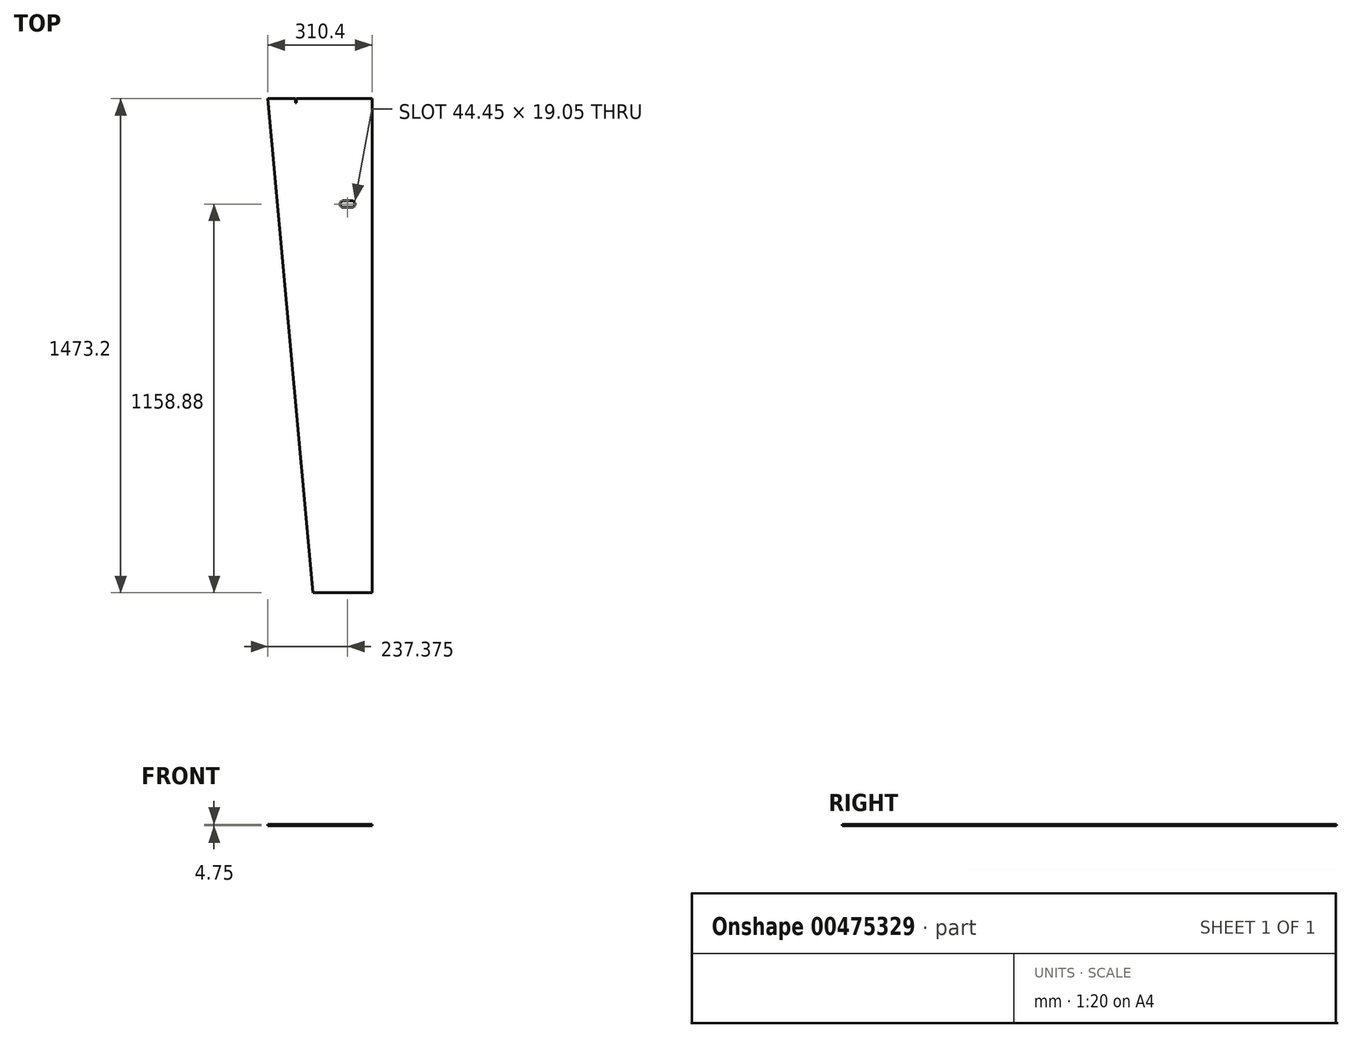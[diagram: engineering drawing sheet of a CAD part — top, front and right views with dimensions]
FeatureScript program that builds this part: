
annotation { "Feature Type Name" : "Feature", "Feature Type Description" : "" }
export const myFeature = defineFeature(function(context is Context, id is Id, definition is map)
    precondition{}
    {
        {
            var Q0;
            Q0=qCreatedBy(makeId("Top.planeOp"),FACE);
            var sketch = newSketch(context, id + "F0", { "sketchPlane" : qUnion([Q0])});
            skLineSegment(sketch, "E0", {"start": v(-176.47, -736.6) * mm, "end": v(-310.4, 736.6) * mm});
            skLineSegment(sketch, "E1", {"start": v(-310.4, 736.6) * mm, "end": v(-228.6, 736.6) * mm});
            skLineSegment(sketch, "E2", {"start": v(0, 736.6) * mm, "end": v(0, -736.6) * mm});
            skLineSegment(sketch, "E3", {"start": v(0, -736.6) * mm, "end": v(-176.47, -736.6) * mm});
            skLineSegment(sketch, "E4.bottom", {"start": v(-85.73, 431.8) * mm, "end": v(-60.33, 431.8) * mm});
            skLineSegment(sketch, "E4.top", {"start": v(-85.73, 412.75) * mm, "end": v(-60.33, 412.75) * mm});
            skArc(sketch, "E5", {"start": v(-85.73, 431.8) * mm, "mid": v(-95.25, 422.27) * mm, "end": v(-85.73, 412.75) * mm});
            skArc(sketch, "E6", {"start": v(-60.33, 412.75) * mm, "mid": v(-50.8, 422.27) * mm, "end": v(-60.33, 431.8) * mm});
            skLineSegment(sketch, "E7", {"start": v(-226.06, 736.6) * mm, "end": v(-226.06, 723.9) * mm});
            skLineSegment(sketch, "E8", {"start": v(-228.6, 723.9) * mm, "end": v(-226.06, 723.9) * mm});
            skLineSegment(sketch, "E9", {"start": v(-228.6, 723.9) * mm, "end": v(-228.6, 736.6) * mm});
            skLineSegment(sketch, "E10.trimOffspring", {"start": v(-226.06, 736.6) * mm, "end": v(0, 736.6) * mm});
            skSolve(sketch);
        }
        {
            var Q0;
            Q0=makeQuery(id+"F0.imprint","IMPRINT",FACE,{"disambiguationData":[TD([[makeQuery(id+"F0.imprint","IMPRINT",EDGE,{"derivedFrom":sQuery(id+"F0.wireOp",EDGE,"E0")}),-1.0]])]});
            extrude(context, id + "F1", {"entities" : qUnion([Q0]), "oppositeDirection" : true, "depth" : 4.75 * mm});
        }
    });
